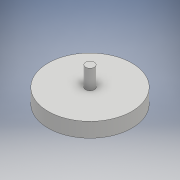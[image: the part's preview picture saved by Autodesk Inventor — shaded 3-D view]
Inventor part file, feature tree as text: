
AUTODESK INVENTOR PART (.ipt)
format: ipt  version: 2017 SP1 (Build 210196100, 196)  size: 104,448 bytes
history: native  units: mm
features: extrude x3, sketch x3
ambient origin geometry x8: Origin, YZ Plane, XZ Plane, XY Plane, X Axis, Y Axis, Z Axis, Center Point
bodies: Solide1 (feature_tree)
feature tree (6):
  extrude  "Extrusion1"  Depth=15.0mm TaperAngle=0.0deg
  extrude  "Extrusion2"  Depth=86.0mm
  extrude  "Extrusion3"  Depth=9.0mm
  sketch  "Esquisse1"
  sketch  "Esquisse2"
  sketch  "Esquisse3"
